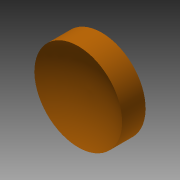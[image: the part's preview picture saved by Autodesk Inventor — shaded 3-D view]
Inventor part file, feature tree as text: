
AUTODESK INVENTOR PART (.ipt)
format: ipt  version: 2013 (Build 170138000, 138)  size: 116,736 bytes
history: native  units: in
note: dims shown in document units (in); Inventor stores cm internally (conversion verified against a paired STEP export)
features: revolve x1, sketch x1
ambient origin geometry x8: Origin, YZ Plane, XZ Plane, XY Plane, X Axis, Y Axis, Z Axis, Center Point
bodies: Solid1 (feature_tree)
feature tree (2):
  revolve  "Revolution1"  Angle=90.0deg
  sketch  "Sketch1"  dims[d0=0.025in d1=90.0deg d2=0.0935in d3=0.05in d4=90.0deg]
